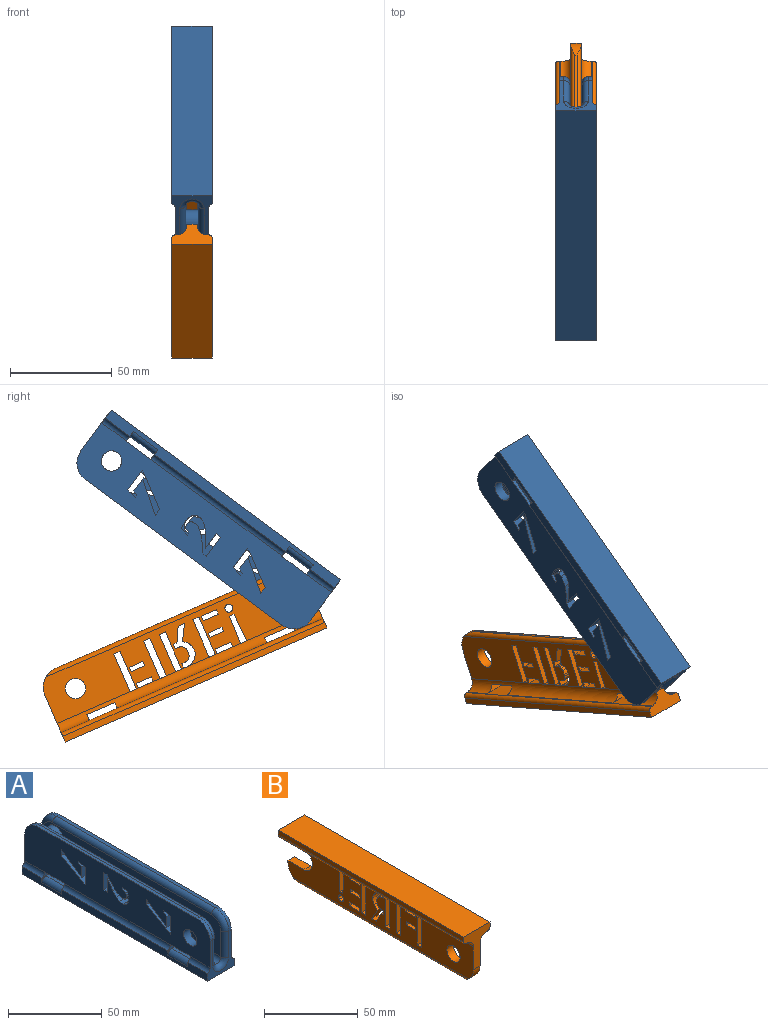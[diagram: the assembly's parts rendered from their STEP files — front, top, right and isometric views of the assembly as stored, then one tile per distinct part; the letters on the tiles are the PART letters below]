
ASSEMBLY  parts=2 mates=1
PART A: 133 faces, bbox 20x141.6x36.6 mm
  f0: plane 134x24mm, normal (1,0,0), area 2748.9mm2, adj f13,f14,f17,f28,f29,f32,f81,f82
  f1: plane 140x27.17mm, normal (-1,0,0), area 3423mm2, adj f5,f7,f12,f14,f15,f16,f17,f18
  f2: plane 140x27.17mm, normal (1,0,0), area 3423mm2, adj f5,f7,f11,f20,f21,f22,f23,f24
  f3: plane 134x24mm, normal (-1,0,0), area 2748.9mm2, adj f13,f22,f25,f28,f29,f32,f43,f44
  f4: plane 15x14mm, normal (0,0,1), area 210mm2, adj f18,f19,f23,f24,f39,f41
  f5: plane 25x20mm, normal (0,-1,0), area 162.5mm2, adj f1,f2,f6,f8,f10,f33,f34,f36
  f6: plane 140x5mm, normal (1,0,0), area 610mm2, adj f5,f7,f10,f20,f21,f23,f24,f26
  f7: plane 25x20mm, normal (0,1,0), area 162.5mm2, adj f1,f2,f6,f8,f10,f26,f30,f35
  f8: plane 140x5mm, normal (-1,0,0), area 610mm2, adj f5,f7,f10,f15,f16,f18,f19,f30
  f9: plane 15x14mm, normal (0,0,1), area 210mm2, adj f15,f16,f20,f21,f40,f42
  f10: plane 140x20mm, normal (0,0,-1), area 2800mm2, adj f5,f6,f7,f8
  f11: plane 120x2mm, normal (0,0,1), area 240mm2, adj f2,f35,f36,f127
  f12: plane 120x2mm, normal (0,0,1), area 240mm2, adj f1,f37,f38,f126
  f13: cylinder r=6mm len=12mm, axis (-1,0,0), area 226.2mm2, adj f0,f3
  f14: plane 15x5mm, normal (0,0,-1), area 75mm2, adj f0,f1,f15,f16
  f15: plane 10x6mm, normal (0,1,0), area 20.4mm2, adj f1,f8,f9,f14,f32,f33,f42
  f16: plane 10x6mm, normal (0,-1,0), area 20.4mm2, adj f1,f8,f9,f14,f29,f31,f42
  f17: plane 15x5mm, normal (0,0,-1), area 75mm2, adj f0,f1,f18,f19
  f18: plane 10x6mm, normal (0,-1,0), area 20.4mm2, adj f1,f4,f8,f17,f28,f30,f41
  f19: plane 10x6mm, normal (0,1,0), area 20.4mm2, adj f1,f4,f8,f17,f29,f31,f41
  f20: plane 10x6mm, normal (0,-1,0), area 20.4mm2, adj f2,f6,f9,f22,f27,f29,f40
  f21: plane 10x6mm, normal (0,1,0), area 20.4mm2, adj f2,f6,f9,f22,f32,f34,f40
  f22: plane 15x5mm, normal (0,0,-1), area 75mm2, adj f2,f3,f20,f21
  f23: plane 10x6mm, normal (0,1,0), area 20.4mm2, adj f2,f4,f6,f25,f27,f29,f39
  f24: plane 10x6mm, normal (0,-1,0), area 20.4mm2, adj f2,f4,f6,f25,f26,f28,f39
  f25: plane 15x5mm, normal (0,0,-1), area 75mm2, adj f2,f3,f23,f24
  f26: cylinder r=3mm len=15mm, axis (0,-1,0), area 55.4mm2, adj f2,f6,f7,f24
  f27: cylinder r=3mm len=80mm, axis (0,-1,0), area 295.4mm2, adj f2,f6,f20,f23
  f28: cylinder r=3mm len=12mm, axis (0,-1,0), area 113.1mm2, adj f0,f3,f18,f24,f132
  f29: cylinder r=3mm len=80mm, axis (0,-1,0), area 754mm2, adj f0,f3,f16,f19,f20,f23
  f30: cylinder r=3mm len=15mm, axis (0,-1,0), area 55.4mm2, adj f1,f7,f8,f18
  f31: cylinder r=3mm len=80mm, axis (0,-1,0), area 295.4mm2, adj f1,f8,f16,f19
  f32: cylinder r=3mm len=12mm, axis (0,1,0), area 113.1mm2, adj f0,f3,f15,f21,f121
  f33: cylinder r=3mm len=15mm, axis (0,-1,0), area 55.4mm2, adj f1,f5,f8,f15
  f34: cylinder r=3mm len=15mm, axis (0,-1,0), area 55.4mm2, adj f2,f5,f6,f21
  f35: cylinder r=10mm len=10mm, axis (1,0,0), area 31.4mm2, adj f2,f7,f11,f129
  f36: cylinder r=10mm len=10mm, axis (-1,0,0), area 31.4mm2, adj f2,f5,f11,f125
  f37: cylinder r=10mm len=10mm, axis (1,0,0), area 31.4mm2, adj f1,f7,f12,f128
  f38: cylinder r=10mm len=10mm, axis (-1,0,0), area 31.4mm2, adj f1,f5,f12,f124
  f39: cylinder r=3mm len=15mm, axis (0,-1,0), area 70.7mm2, adj f4,f6,f23,f24
  f40: cylinder r=3mm len=15mm, axis (0,-1,0), area 70.7mm2, adj f6,f9,f20,f21
  f41: cylinder r=3mm len=15mm, axis (0,1,0), area 70.7mm2, adj f4,f8,f18,f19
  f42: cylinder r=3mm len=15mm, axis (0,1,0), area 70.7mm2, adj f8,f9,f15,f16
  f43: plane 5x2.46mm, normal (0,-0.39,-0.92), area 13.3mm2, adj f2,f3,f44,f49
  f44: plane 7.23x5mm, normal (0,-1,0), area 36.1mm2, adj f2,f3,f43,f45
  f45: plane 15.54x10.57mm, normal (0,0.56,0.83), area 94mm2, adj f2,f3,f44,f46
  f46: plane 5x3.53mm, normal (0,-1,0), area 17.7mm2, adj f2,f3,f45,f47
  f47: plane 17.23x10.01mm, normal (0,-0.5,-0.86), area 99.6mm2, adj f2,f3,f46,f48
  f48: plane 5x1.08mm, normal (0,-0.18,-0.98), area 5.5mm2, adj f2,f3,f47,f50
  f49: plane 5x1.19mm, normal (0,-1,0), area 5.9mm2, adj f2,f3,f43,f51
  f50: plane 11.7x5mm, normal (0,1,0), area 58.5mm2, adj f2,f3,f48,f51
  f51: plane 5.23x5mm, normal (0,0.17,0.98), area 26.6mm2, adj f2,f3,f49,f50
  f52: plane 5x2.81mm, normal (0,-0.19,-0.98), area 14.3mm2, adj f2,f3,f53,f69
  f53: plane 9.18x5mm, normal (0,1,0), area 45.9mm2, adj f2,f3,f52,f54
  f54: extruded ~5.84x5mm, area 35.5mm2, adj f2,f3,f53,f55
  f55: extruded ~5x2.79mm, area 19.1mm2, adj f2,f3,f54,f56
  f56: extruded ~5x2.48mm, area 14.7mm2, adj f2,f3,f55,f57
  f57: extruded ~5x2.61mm, area 13.4mm2, adj f2,f3,f56,f58
  f58: extruded ~5x2.9mm, area 16.8mm2, adj f2,f3,f57,f59
  f59: extruded ~5x3.97mm, area 20.9mm2, adj f2,f3,f58,f60
  f60: extruded ~5x2.3mm, area 11.5mm2, adj f2,f3,f59,f61
  f61: extruded ~5x2.22mm, area 11.3mm2, adj f2,f3,f60,f62
  f62: plane 5x4.16mm, normal (0,0.17,0.98), area 21.1mm2, adj f2,f3,f61,f63
  f63: plane 5x1.19mm, normal (0,-1,0), area 5.9mm2, adj f2,f3,f62,f64
  f64: plane 5x2.65mm, normal (0,-0.37,-0.93), area 14.2mm2, adj f2,f3,f63,f65
  f65: extruded ~5x2.17mm, area 11.6mm2, adj f2,f3,f64,f66
  f66: extruded ~5x1.79mm, area 9.8mm2, adj f2,f3,f65,f67
  f67: extruded ~5x2.14mm, area 11.5mm2, adj f2,f3,f66,f68
  f68: extruded ~5x4.98mm, area 27.5mm2, adj f2,f3,f67,f70
  f69: plane 11.6x5mm, normal (0,-1,0), area 58mm2, adj f2,f3,f52,f71
  f70: extruded ~7.37x6.76mm, area 50.1mm2, adj f2,f3,f68,f71
  f71: plane 5x2.58mm, normal (0,0.17,0.99), area 13.1mm2, adj f2,f3,f69,f70
  f72: plane 5x2.46mm, normal (0,-0.39,-0.92), area 13.3mm2, adj f2,f3,f73,f78
  f73: plane 7.23x5mm, normal (0,-1,0), area 36.1mm2, adj f2,f3,f72,f74
  f74: plane 15.54x10.57mm, normal (0,0.56,0.83), area 94mm2, adj f2,f3,f73,f75
  f75: plane 5x3.53mm, normal (0,-1,0), area 17.7mm2, adj f2,f3,f74,f76
  f76: plane 17.23x10.01mm, normal (0,-0.5,-0.86), area 99.6mm2, adj f2,f3,f75,f77
  f77: plane 5x1.08mm, normal (0,-0.18,-0.98), area 5.5mm2, adj f2,f3,f76,f79
  f78: plane 5x1.19mm, normal (0,-1,0), area 5.9mm2, adj f2,f3,f72,f80
  f79: plane 11.7x5mm, normal (0,1,0), area 58.5mm2, adj f2,f3,f77,f80
  f80: plane 5.23x5mm, normal (0,0.17,0.98), area 26.6mm2, adj f2,f3,f78,f79
  f81: plane 5x1.19mm, normal (0,-1,0), area 5.9mm2, adj f0,f1,f82,f89
  f82: plane 5x2.46mm, normal (0,-0.39,0.92), area 13.3mm2, adj f0,f1,f81,f83
  f83: plane 7.23x5mm, normal (0,-1,0), area 36.1mm2, adj f0,f1,f82,f84
  f84: plane 15.54x10.57mm, normal (0,0.56,-0.83), area 94mm2, adj f0,f1,f83,f85
  f85: plane 5x3.53mm, normal (0,-1,0), area 17.7mm2, adj f0,f1,f84,f86
  f86: plane 17.23x10.01mm, normal (0,-0.5,0.86), area 99.6mm2, adj f0,f1,f85,f87
  f87: plane 5x1.08mm, normal (0,-0.18,0.98), area 5.5mm2, adj f0,f1,f86,f88
  f88: plane 11.7x5mm, normal (0,1,0), area 58.5mm2, adj f0,f1,f87,f89
  f89: plane 5.23x5mm, normal (0,0.17,-0.98), area 26.6mm2, adj f0,f1,f81,f88
  f90: plane 11.6x5mm, normal (0,-1,0), area 58mm2, adj f0,f1,f91,f109
  f91: plane 5x2.81mm, normal (0,-0.19,0.98), area 14.3mm2, adj f0,f1,f90,f92
  f92: plane 9.18x5mm, normal (0,1,0), area 45.9mm2, adj f0,f1,f91,f93
  f93: extruded ~5.84x5mm, area 35.5mm2, adj f0,f1,f92,f94
  f94: extruded ~5x2.79mm, area 19.1mm2, adj f0,f1,f93,f95
  f95: extruded ~5x2.48mm, area 14.7mm2, adj f0,f1,f94,f96
  f96: extruded ~5x2.61mm, area 13.4mm2, adj f0,f1,f95,f97
  f97: extruded ~5x2.9mm, area 16.8mm2, adj f0,f1,f96,f98
  f98: extruded ~5x3.97mm, area 20.9mm2, adj f0,f1,f97,f99
  f99: extruded ~5x2.3mm, area 11.5mm2, adj f0,f1,f98,f100
  f100: extruded ~5x2.22mm, area 11.3mm2, adj f0,f1,f99,f101
  f101: plane 5x4.16mm, normal (0,0.17,-0.98), area 21.1mm2, adj f0,f1,f100,f102
  f102: plane 5x1.19mm, normal (0,-1,0), area 5.9mm2, adj f0,f1,f101,f103
  f103: plane 5x2.65mm, normal (0,-0.37,0.93), area 14.2mm2, adj f0,f1,f102,f104
  f104: extruded ~5x2.17mm, area 11.6mm2, adj f0,f1,f103,f105
  f105: extruded ~5x1.79mm, area 9.8mm2, adj f0,f1,f104,f106
  f106: extruded ~5x2.14mm, area 11.5mm2, adj f0,f1,f105,f107
  f107: extruded ~5x4.98mm, area 27.5mm2, adj f0,f1,f106,f108
  f108: extruded ~7.37x6.76mm, area 50.1mm2, adj f0,f1,f107,f109
  f109: plane 5x2.58mm, normal (0,0.17,-0.99), area 13.1mm2, adj f0,f1,f90,f108
  f110: plane 5x1.19mm, normal (0,-1,0), area 5.9mm2, adj f0,f1,f111,f118
  f111: plane 5x2.46mm, normal (0,-0.39,0.92), area 13.3mm2, adj f0,f1,f110,f112
  f112: plane 7.23x5mm, normal (0,-1,0), area 36.1mm2, adj f0,f1,f111,f113
  f113: plane 15.54x10.57mm, normal (0,0.56,-0.83), area 94mm2, adj f0,f1,f112,f114
  f114: plane 5x3.53mm, normal (0,-1,0), area 17.7mm2, adj f0,f1,f113,f115
  f115: plane 17.23x10.01mm, normal (0,-0.5,0.86), area 99.6mm2, adj f0,f1,f114,f116
  f116: plane 5x1.08mm, normal (0,-0.18,0.98), area 5.5mm2, adj f0,f1,f115,f117
  f117: plane 11.7x5mm, normal (0,1,0), area 58.5mm2, adj f0,f1,f116,f118
  f118: plane 5.23x5mm, normal (0,0.17,-0.98), area 26.6mm2, adj f0,f1,f110,f117
  f119: cylinder r=5mm len=10mm, axis (-1,0,0), area 157.1mm2, adj f2,f3
  f120: cylinder r=5mm len=10mm, axis (-1,0,0), area 157.1mm2, adj f0,f1
  f121: torus R=6mm, axis (0,-1,0), area 60.6mm2, adj f5,f32,f122,f123
  f122: cylinder r=3mm len=17mm, axis (0,0,-1), area 80.1mm2, adj f0,f5,f121,f124
  f123: cylinder r=3mm len=17mm, axis (0,0,1), area 80.1mm2, adj f3,f5,f121,f125
  f124: torus R=7mm, axis (1,0,0), area 66mm2, adj f0,f38,f122,f126
  f125: torus R=7mm, axis (1,0,0), area 66mm2, adj f3,f36,f123,f127
  f126: cylinder r=3mm len=120mm, axis (0,-1,0), area 565.5mm2, adj f0,f12,f124,f128
  f127: cylinder r=3mm len=120mm, axis (0,1,0), area 565.5mm2, adj f3,f11,f125,f129
  f128: torus R=7mm, axis (1,0,0), area 66mm2, adj f0,f37,f126,f130
  f129: torus R=7mm, axis (1,0,0), area 66mm2, adj f3,f35,f127,f131
  f130: cylinder r=3mm len=17mm, axis (0,0,1), area 80.1mm2, adj f0,f7,f128,f132
  f131: cylinder r=3mm len=17mm, axis (0,0,-1), area 80.1mm2, adj f3,f7,f129,f132
  f132: torus R=6mm, axis (0,-1,0), area 60.6mm2, adj f7,f28,f130,f131
PART B: 101 faces, bbox 20x140x35 mm
  f0: plane 140x23mm, normal (1,0,0), area 2413.6mm2, adj f2,f3,f5,f10,f17,f18,f19,f20
  f1: plane 140x23mm, normal (-1,0,0), area 2414.2mm2, adj f2,f3,f5,f10,f17,f18,f19,f20
  f2: plane 5x1.5mm, normal (0,1,0), area 7.5mm2, adj f0,f1,f19,f20
  f3: plane 20x10.5mm, normal (0,1,0), area 136.5mm2, adj f0,f1,f4,f6,f7,f8,f17,f22
  f4: plane 140x3mm, normal (-1,0,0), area 420mm2, adj f3,f5,f7,f24
  f5: plane 25x20mm, normal (0,-1,0), area 209mm2, adj f0,f1,f4,f6,f7,f8,f21,f22
  f6: plane 140x3mm, normal (1,0,0), area 420mm2, adj f3,f5,f7,f25
  f7: plane 140x20mm, normal (0,0,1), area 2800mm2, adj f3,f4,f5,f6
  f8: plane 140x16mm, normal (0,0,-1), area 590mm2, adj f3,f5,f11,f13,f14,f15,f22,f23
  f9: plane 120x1mm, normal (0,0,-1), area 120mm2, adj f20,f21,f26,f27
  f10: cylinder r=5mm len=10mm, axis (-1,0,0), area 157.1mm2, adj f0,f1
  f11: plane 15x3mm, normal (0,1,0), area 25.2mm2, adj f8,f12,f22,f23
  f12: plane 15x5.84mm, normal (0,0,1), area 87.5mm2, adj f11,f13,f22,f23
  f13: plane 15x3mm, normal (0,-1,0), area 25.2mm2, adj f8,f12,f22,f23
  f14: plane 15x3mm, normal (0,-1,0), area 25.2mm2, adj f8,f16,f22,f23
  f15: plane 15x3mm, normal (0,1,0), area 25.2mm2, adj f8,f16,f22,f23
  f16: plane 15x5.84mm, normal (0,0,1), area 87.5mm2, adj f14,f15,f22,f23
  f17: plane 12x5mm, normal (0,0,-1), area 60mm2, adj f0,f1,f3,f18
  f18: cylinder r=6.5mm len=13mm, axis (1,0,0), area 102.1mm2, adj f0,f1,f17,f19
  f19: plane 12x5mm, normal (0,0,1), area 60mm2, adj f0,f1,f2,f18
  f20: cylinder r=10mm len=10mm, axis (-1,0,0), area 65.7mm2, adj f0,f1,f2,f9,f26,f27
  f21: cylinder r=10mm len=10mm, axis (1,0,0), area 65.7mm2, adj f0,f1,f5,f9,f26,f27
  f22: cylinder r=5mm len=140mm, axis (0,1,0), area 926mm2, adj f0,f3,f5,f8,f11,f12,f13,f14
  f23: cylinder r=5mm len=140mm, axis (0,-1,0), area 925.7mm2, adj f1,f3,f5,f8,f11,f12,f13,f14
  f24: cylinder r=2mm len=140mm, axis (0,-1,0), area 439.8mm2, adj f3,f4,f5,f8
  f25: cylinder r=2mm len=140mm, axis (0,1,0), area 439.8mm2, adj f3,f5,f6,f8
  f26: cylinder r=2mm len=132mm, axis (0,-1,0), area 395.8mm2, adj f0,f9,f20,f21
  f27: cylinder r=2mm len=132mm, axis (0,1,0), area 395.8mm2, adj f1,f9,f20,f21
  f28: plane 5x2.47mm, normal (0,-1,0), area 12.4mm2, adj f0,f1,f29,f31
  f29: plane 8.08x5mm, normal (0,0,-1), area 40.4mm2, adj f1,f22,f28,f30
  f30: plane 5x2.47mm, normal (0,1,0), area 12.3mm2, adj f0,f1,f29,f31
  f31: plane 8.08x5mm, normal (0,0,1), area 40.4mm2, adj f0,f1,f28,f30
  f32: plane 5x3.31mm, normal (0,0,1), area 16.5mm2, adj f0,f1,f33,f35
  f33: plane 20x5mm, normal (0,-1,0), area 100mm2, adj f0,f1,f32,f34
  f34: plane 5x3.31mm, normal (0,0,-1), area 16.5mm2, adj f1,f22,f33,f35
  f35: plane 20x5mm, normal (0,1,0), area 100mm2, adj f0,f1,f32,f34
  f36: plane 5x3.26mm, normal (0,0,-1), area 16.3mm2, adj f1,f22,f37,f39
  f37: plane 20x5mm, normal (0,1,0), area 100mm2, adj f0,f1,f36,f38
  f38: plane 5x3.26mm, normal (0,0,1), area 16.3mm2, adj f0,f1,f37,f39
  f39: plane 20x5mm, normal (0,-1,0), area 100mm2, adj f0,f1,f36,f38
  f40: plane 5x3.31mm, normal (0,0,-1), area 16.5mm2, adj f1,f22,f41,f43
  f41: plane 20x5mm, normal (0,1,0), area 100mm2, adj f0,f1,f40,f42
  f42: plane 5x3.31mm, normal (0,0,1), area 16.5mm2, adj f0,f1,f41,f43
  f43: plane 20x5mm, normal (0,-1,0), area 100mm2, adj f0,f1,f40,f42
  f44: plane 5x2.47mm, normal (0,-1,0), area 12.4mm2, adj f0,f1,f45,f47
  f45: plane 8.08x5mm, normal (0,0,-1), area 40.4mm2, adj f1,f22,f44,f46
  f46: plane 5x2.47mm, normal (0,1,0), area 12.3mm2, adj f0,f1,f45,f47
  f47: plane 8.08x5mm, normal (0,0,1), area 40.4mm2, adj f0,f1,f44,f46
  f48: plane 5x2.42mm, normal (0,0,1), area 12.1mm2, adj f0,f1,f49,f51
  f49: plane 14.47x5mm, normal (0,-1,0.03), area 72.3mm2, adj f0,f1,f48,f50
  f50: plane 5x3.31mm, normal (0,0,-1), area 16.6mm2, adj f1,f22,f49,f51
  f51: plane 14.47x5mm, normal (0,1,0.03), area 72.3mm2, adj f0,f1,f48,f50
  f52: plane 5x3.31mm, normal (0,0,-1), area 16.5mm2, adj f1,f22,f53,f55
  f53: plane 20x5mm, normal (0,1,0), area 100mm2, adj f0,f1,f52,f54
  f54: plane 5x3.31mm, normal (0,0,1), area 16.5mm2, adj f0,f1,f53,f55
  f55: plane 20x5mm, normal (0,-1,0), area 100mm2, adj f0,f1,f52,f54
  f56: plane 7.24x5mm, normal (0,0,1), area 36.2mm2, adj f0,f1,f57,f59
  f57: plane 5x2.23mm, normal (0,-1,0), area 11.1mm2, adj f0,f1,f56,f58
  f58: plane 7.24x5mm, normal (0,0,-1), area 36.2mm2, adj f0,f1,f57,f59
  f59: plane 5x2.23mm, normal (0,1,0), area 11.1mm2, adj f0,f1,f56,f58
  f60: plane 5x3.45mm, normal (0,0,1), area 17.2mm2, adj f0,f1,f61,f84
  f61: plane 7.87x5mm, normal (0,-0.87,-0.5), area 45.5mm2, adj f0,f1,f60,f62
  f62: extruded ~5x2.71mm, area 17.9mm2, adj f0,f1,f61,f63
  f63: extruded ~5x3.69mm, area 19.4mm2, adj f0,f1,f62,f64
  f64: extruded ~5x2.59mm, area 13.5mm2, adj f0,f1,f63,f65
  f65: extruded ~5x1.97mm, area 12.8mm2, adj f0,f1,f64,f66
  f66: extruded ~5x2.24mm, area 12.8mm2, adj f0,f1,f65,f67
  f67: extruded ~5x2.52mm, area 12.8mm2, adj f0,f1,f66,f68
  f68: plane 5x1.38mm, normal (0,0,-1), area 6.9mm2, adj f1,f22,f67,f69
  f69: plane 5x2.47mm, normal (0,1,0), area 12.3mm2, adj f0,f1,f68,f70
  f70: plane 5x1.33mm, normal (0,0,1), area 6.6mm2, adj f0,f1,f69,f71
  f71: extruded ~5x2.01mm, area 10.3mm2, adj f0,f1,f70,f72
  f72: extruded ~5x1.18mm, area 7.7mm2, adj f0,f1,f71,f73
  f73: extruded ~5x1.22mm, area 6.7mm2, adj f0,f1,f72,f74
  f74: extruded ~5x1.13mm, area 5.7mm2, adj f0,f1,f73,f75
  f75: extruded ~5x2.05mm, area 10.4mm2, adj f0,f1,f74,f76
  f76: extruded ~5x1.29mm, area 7.6mm2, adj f0,f1,f75,f77
  f77: extruded ~5x1.09mm, area 6.4mm2, adj f0,f1,f76,f78
  f78: extruded ~5x1.19mm, area 6.1mm2, adj f0,f1,f77,f79
  f79: plane 5x1.84mm, normal (0,0,-1), area 9.2mm2, adj f0,f1,f78,f80
  f80: plane 5x2.39mm, normal (0,1,0), area 11.9mm2, adj f0,f1,f79,f81
  f81: plane 5x1.52mm, normal (0,0,1), area 7.6mm2, adj f0,f1,f80,f82
  f82: extruded ~5x0.28mm, area 1.4mm2, adj f0,f1,f81,f83
  f83: extruded ~5x0.18mm, area 0.9mm2, adj f0,f1,f82,f84
  f84: plane 7.24x5mm, normal (0,0.89,0.46), area 40.8mm2, adj f0,f1,f60,f83
  f85: plane 7.24x5mm, normal (0,0,1), area 36.2mm2, adj f0,f1,f86,f88
  f86: plane 5x2.23mm, normal (0,-1,0), area 11.1mm2, adj f0,f1,f85,f87
  f87: plane 7.24x5mm, normal (0,0,-1), area 36.2mm2, adj f0,f1,f86,f88
  f88: plane 5x2.23mm, normal (0,1,0), area 11.1mm2, adj f0,f1,f85,f87
  f89: plane 8.08x5mm, normal (0,0,-1), area 40.4mm2, adj f0,f1,f90,f92
  f90: plane 5x2.47mm, normal (0,1,0), area 12.3mm2, adj f0,f1,f89,f91
  f91: plane 8.08x5mm, normal (0,0,1), area 40.4mm2, adj f0,f1,f90,f92
  f92: plane 5x2.47mm, normal (0,-1,0), area 12.3mm2, adj f0,f1,f89,f91
  f93: extruded ~5x1.38mm, area 7.7mm2, adj f0,f1,f94,f100
  f94: extruded ~5x1.37mm, area 7.6mm2, adj f0,f1,f93,f95
  f95: extruded ~5x1.38mm, area 7.6mm2, adj f0,f1,f94,f96
  f96: extruded ~5x1.36mm, area 7.5mm2, adj f0,f1,f95,f97
  f97: extruded ~5x1.37mm, area 7.6mm2, adj f0,f1,f96,f98
  f98: extruded ~5x1.38mm, area 7.6mm2, adj f0,f1,f97,f99
  f99: extruded ~5x1.37mm, area 7.6mm2, adj f0,f1,f98,f100
  f100: extruded ~5x1.38mm, area 7.7mm2, adj f0,f1,f93,f99
PLACE A rot(axis=(-1,0,0),143.5deg) t=(4.34,15.52,-33.51)mm
PLACE B rot(axis=(1,0,0),156.5deg) t=(4.34,46.91,-88.32)mm
MATE revolute B.f18 <-> A.f13  axis (-1,0,0) through (4.34,-16.25,-88.09)mm
